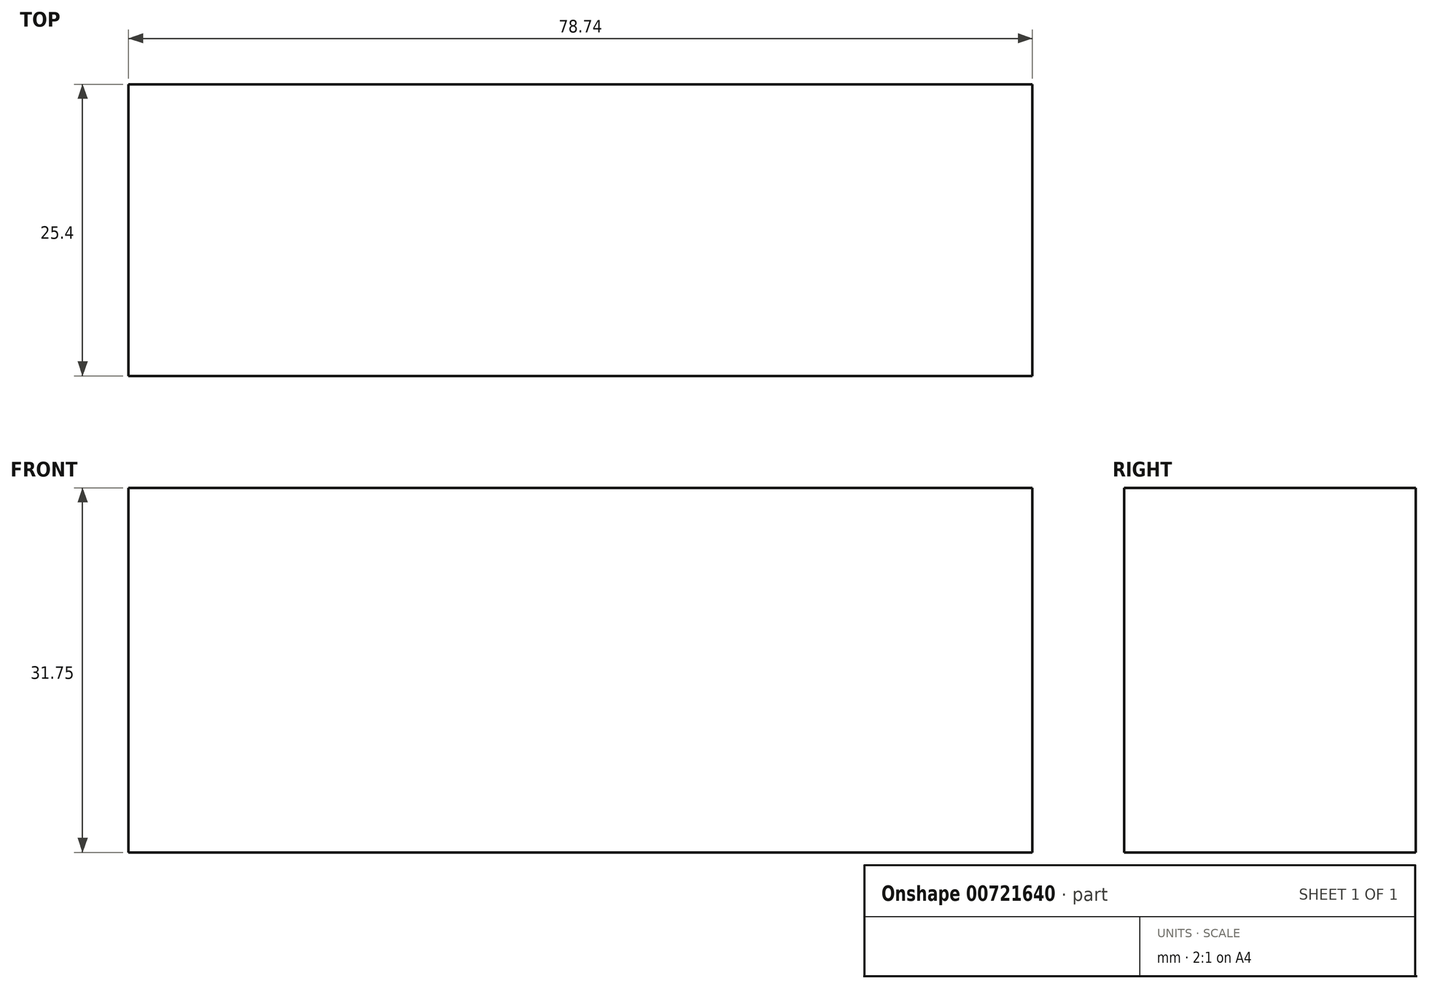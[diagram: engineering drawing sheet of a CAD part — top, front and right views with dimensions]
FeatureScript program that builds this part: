
annotation { "Feature Type Name" : "Feature", "Feature Type Description" : "" }
export const myFeature = defineFeature(function(context is Context, id is Id, definition is map)
    precondition{}
    {
        {
            var Q0;
            Q0=qCreatedBy(makeId("Front.planeOp"),FACE);
            var sketch = newSketch(context, id + "F0", { "sketchPlane" : qUnion([Q0])});
            skLineSegment(sketch, "E0.bottom", {"start": v(0, 0) * mm, "end": v(78.74, 0) * mm});
            skLineSegment(sketch, "E0.top", {"start": v(0, 31.75) * mm, "end": v(78.74, 31.75) * mm});
            skLineSegment(sketch, "E0.left", {"start": v(0, 0) * mm, "end": v(0, 31.75) * mm});
            skLineSegment(sketch, "E0.right", {"start": v(78.74, 0) * mm, "end": v(78.74, 31.75) * mm});
            skSolve(sketch);
        }
        {
            var Q0;
            Q0=makeQuery(id+"F0.imprint","IMPRINT",FACE,{"disambiguationData":[TD([[makeQuery(id+"F0.imprint","IMPRINT",EDGE,{"derivedFrom":sQuery(id+"F0.wireOp",EDGE,"E0.bottom")}),1.0]])]});
            extrude(context, id + "F1", {"entities" : qUnion([Q0]), "depth" : 25.4 * mm, "offsetDistance" : 25.4 * mm});
        }
    });
